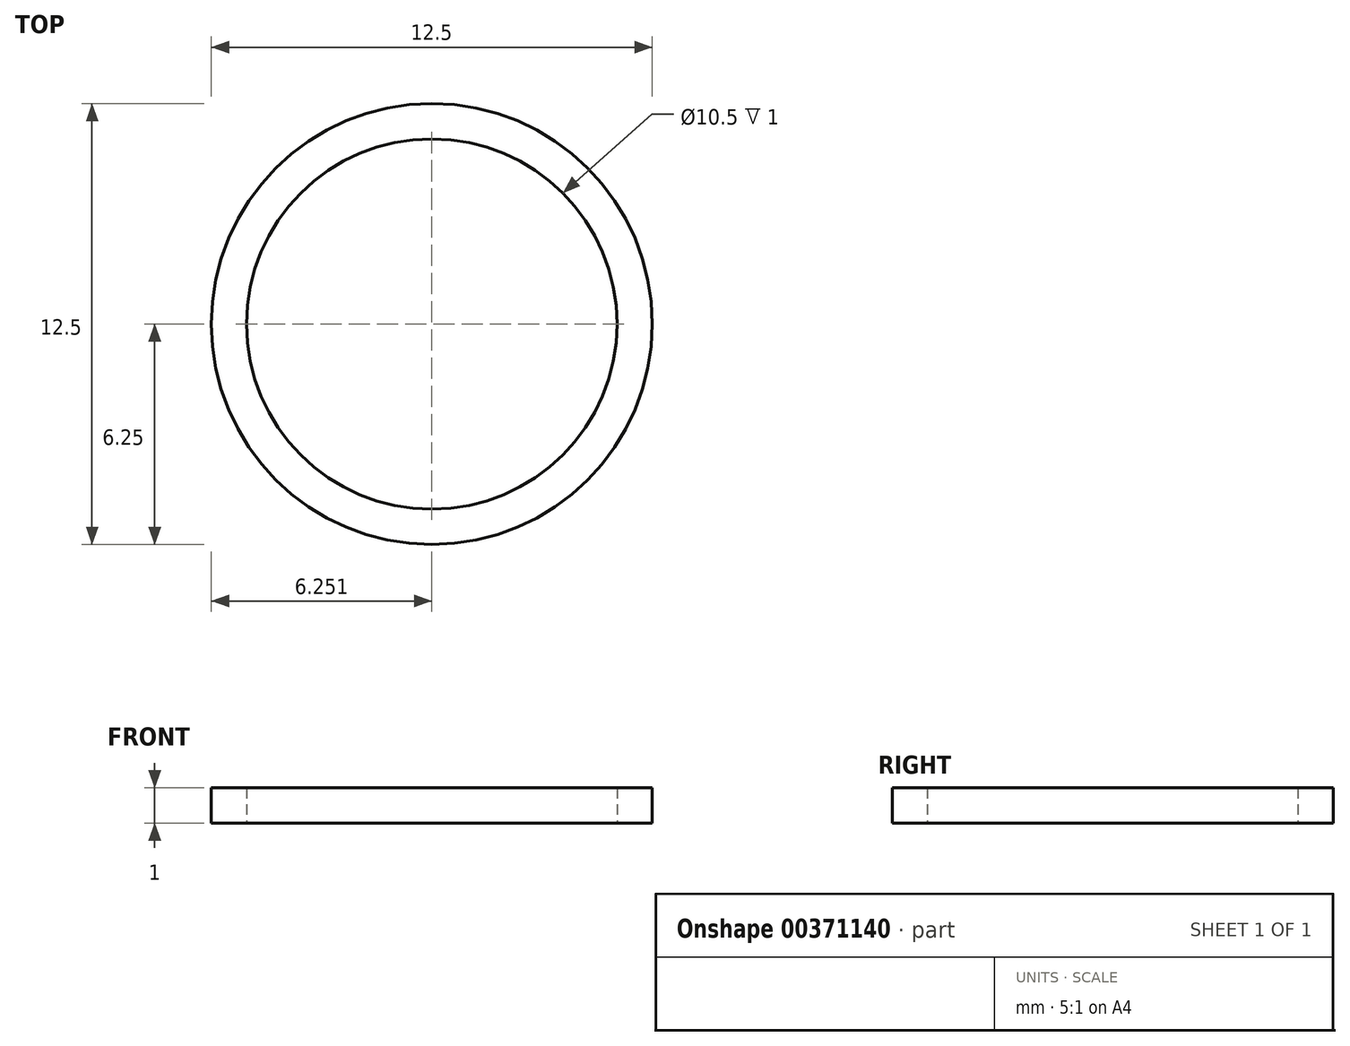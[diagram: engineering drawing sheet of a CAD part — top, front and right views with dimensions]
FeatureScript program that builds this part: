
annotation { "Feature Type Name" : "Feature", "Feature Type Description" : "" }
export const myFeature = defineFeature(function(context is Context, id is Id, definition is map)
    precondition{}
    {
        {
            var Q0;
            Q0=qCreatedBy(makeId("Top.planeOp"),FACE);
            var sketch = newSketch(context, id + "F0", { "sketchPlane" : qUnion([Q0])});
            skCircle(sketch, "E0", {"center": v(-16.48, 0) * mm, "radius": 5.25 * mm});
            skCircle(sketch, "E1", {"center": v(-16.48, 0) * mm, "radius": 6.25 * mm});
            skSolve(sketch);
        }
        {
            var Q0;
            Q0 = qSketchRegion(id + "F0", true);
            extrude(context, id + "F1", {"entities" : qUnion([Q0]), "depth" : 1 * mm});
        }
    });
